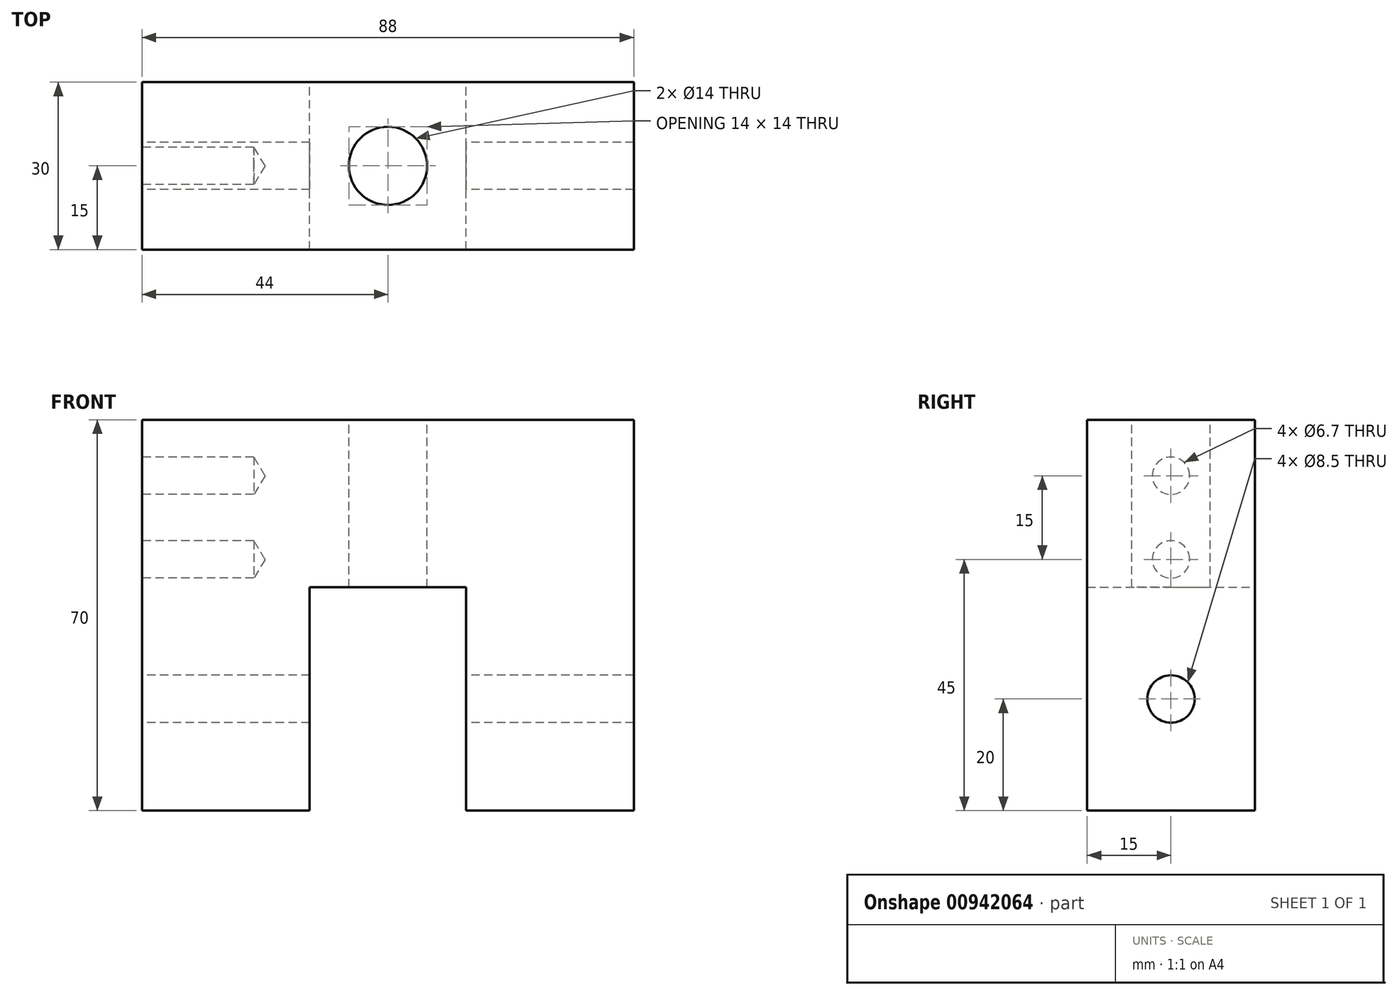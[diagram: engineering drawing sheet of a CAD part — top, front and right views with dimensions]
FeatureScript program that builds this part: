
annotation { "Feature Type Name" : "Feature", "Feature Type Description" : "" }
export const myFeature = defineFeature(function(context is Context, id is Id, definition is map)
    precondition{}
    {
        {
            var Q0;
            Q0=qCreatedBy(makeId("Front.planeOp"),FACE);
            var sketch = newSketch(context, id + "F0", { "sketchPlane" : qUnion([Q0])});
            skLineSegment(sketch, "E0.top", {"start": v(14, 20) * mm, "end": v(-14, 20) * mm});
            skLineSegment(sketch, "E0.left", {"start": v(14, -20) * mm, "end": v(14, 20) * mm});
            skLineSegment(sketch, "E0.right", {"start": v(-14, -20) * mm, "end": v(-14, 20) * mm});
            skPoint(sketch, "E0.middle", {"position": v(0, 0) * mm});
            skLineSegment(sketch, "E1.bottom", {"start": v(-44, -20) * mm, "end": v(-14, -20) * mm});
            skLineSegment(sketch, "E1.top", {"start": v(-44, 50) * mm, "end": v(44, 50) * mm});
            skLineSegment(sketch, "E1.left", {"start": v(-44, -20) * mm, "end": v(-44, 50) * mm});
            skLineSegment(sketch, "E1.right", {"start": v(44, -20) * mm, "end": v(44, 50) * mm});
            skLineSegment(sketch, "E2.trimOffspring", {"start": v(14, -20) * mm, "end": v(44, -20) * mm});
            skSolve(sketch);
        }
        {
            var Q0;
            Q0=makeQuery(id+"F0.imprint","IMPRINT",FACE,{"disambiguationData":[TD([[makeQuery(id+"F0.imprint","IMPRINT",EDGE,{"derivedFrom":sQuery(id+"F0.wireOp",EDGE,"E0.top")}),-1.0]])]});
            extrude(context, id + "F1", {"entities" : qUnion([Q0]), "depth" : 30 * mm, "offsetDistance" : 25 * mm});
        }
        {
            var Q0;
            Q0=makeQuery(id+"F1.opExtrude","SWEPT_FACE",FACE,{"disambiguationData":[OSD([sQuery(id+"F0.wireOp",EDGE,"E1.left")])]});
            var sketch = newSketch(context, id + "F2", { "sketchPlane" : qUnion([Q0])});
            skPoint(sketch, "E3", {"position": v(15, 40) * mm});
            skPoint(sketch, "E4", {"position": v(15, 25) * mm});
            skSolve(sketch);
        }
        {
            var Q0;
            Q0=sQuery(id+"F2.wireOp",VERTEX,"E3");
            var Q1;
            Q1=sQuery(id+"F2.wireOp",VERTEX,"E4");
            var Q2;
            Q2=makeQuery(id+"F1.opExtrude","SWEPT_BODY",BODY,{"disambiguationData":[OSD([sQuery(id+"F0.wireOp",EDGE,"E0.top"),sQuery(id+"F0.wireOp",EDGE,"E0.left"),sQuery(id+"F0.wireOp",EDGE,"E0.right"),sQuery(id+"F0.wireOp",EDGE,"E1.bottom"),sQuery(id+"F0.wireOp",EDGE,"E1.top"),sQuery(id+"F0.wireOp",EDGE,"E1.left"),sQuery(id+"F0.wireOp",EDGE,"E1.right"),sQuery(id+"F0.wireOp",EDGE,"E2.trimOffspring")])]});
            hole(context, id + "F3", {"style" : HoleStyle.SIMPLE, "endStyle" : HoleEndStyle.BLIND, "holeDiameter" : 6.7 * mm, "majorDiameter" : 5 * mm, "holeDepth" : 20 * mm, "isTappedThrough" : true, "tappedDepth" : 12 * mm, "tapClearance" : 3, "locations" : qUnion([Q0, Q1]), "scope" : qUnion([Q2])});
        }
        {
            var Q0;
            Q0=makeQuery(id+"F1.opExtrude","SWEPT_FACE",FACE,{"disambiguationData":[OSD([sQuery(id+"F0.wireOp",EDGE,"E1.top")])]});
            var Q1;
            Q1=makeQuery(id+"F1.opExtrude","SWEPT_FACE",FACE,{"disambiguationData":[OSD([sQuery(id+"F0.wireOp",EDGE,"E1.top")])]});
            var sketch = newSketch(context, id + "F4", { "sketchPlane" : qUnion([Q0, Q1])});
            skPoint(sketch, "E5", {"position": v(0, -15) * mm});
            skSolve(sketch);
        }
        {
            var Q0;
            Q0=sQuery(id+"F4.wireOp",VERTEX,"E5");
            var Q1;
            Q1=makeQuery(id+"F1.opExtrude","SWEPT_BODY",BODY,{"disambiguationData":[OSD([sQuery(id+"F0.wireOp",EDGE,"E0.top"),sQuery(id+"F0.wireOp",EDGE,"E0.left"),sQuery(id+"F0.wireOp",EDGE,"E0.right"),sQuery(id+"F0.wireOp",EDGE,"E1.bottom"),sQuery(id+"F0.wireOp",EDGE,"E1.top"),sQuery(id+"F0.wireOp",EDGE,"E1.left"),sQuery(id+"F0.wireOp",EDGE,"E1.right"),sQuery(id+"F0.wireOp",EDGE,"E2.trimOffspring")])]});
            hole(context, id + "F5", {"style" : HoleStyle.SIMPLE, "endStyle" : HoleEndStyle.THROUGH, "holeDiameter" : 14 * mm, "majorDiameter" : 5 * mm, "isTappedThrough" : true, "tappedDepth" : 12 * mm, "tapClearance" : 3, "locations" : qUnion([Q0]), "scope" : qUnion([Q1])});
        }
        {
            var Q0;
            Q0=makeQuery(id+"F1.opExtrude","SWEPT_FACE",FACE,{"disambiguationData":[OSD([sQuery(id+"F0.wireOp",EDGE,"E1.left")])]});
            var sketch = newSketch(context, id + "F6", { "sketchPlane" : qUnion([Q0])});
            skPoint(sketch, "E6", {"position": v(15, 0) * mm});
            skSolve(sketch);
        }
        {
            var Q0;
            Q0=sQuery(id+"F6.wireOp",VERTEX,"E6");
            var Q1;
            Q1=makeQuery(id+"F1.opExtrude","SWEPT_BODY",BODY,{"disambiguationData":[OSD([sQuery(id+"F0.wireOp",EDGE,"E0.top"),sQuery(id+"F0.wireOp",EDGE,"E0.left"),sQuery(id+"F0.wireOp",EDGE,"E0.right"),sQuery(id+"F0.wireOp",EDGE,"E1.bottom"),sQuery(id+"F0.wireOp",EDGE,"E1.top"),sQuery(id+"F0.wireOp",EDGE,"E1.left"),sQuery(id+"F0.wireOp",EDGE,"E1.right"),sQuery(id+"F0.wireOp",EDGE,"E2.trimOffspring")])]});
            hole(context, id + "F7", {"style" : HoleStyle.SIMPLE, "endStyle" : HoleEndStyle.THROUGH, "holeDiameter" : 8.5 * mm, "majorDiameter" : 5 * mm, "isTappedThrough" : true, "tappedDepth" : 12 * mm, "tapClearance" : 3, "locations" : qUnion([Q0]), "scope" : qUnion([Q1])});
        }
    });
